# Revit family: Wind_Turbine
name_source: partatom
category: Electrical Equipment
units: mm (PartAtom-declared; Revit-internal decimal feet)

## family parameters
Always vertical = Yes
Classification Number = 23.80.10.11
Cut with Voids When Loaded = No
Maintain Annotation Orientation = No
Panel Configuration = Two Columns, Circuits Across
Part Type = Panelboard
Room Calculation Point = No
Round Connector Dimension = Use Diameter
Shared = No
Work Plane-Based = No

## types (1)
- 3600KW
    Assembly Code = D5090
    Blade Material = ARCAT - Plastic - Glass-Fiber Reinforced - White
    BldCrv = 97' - 4 7/8"
    Construction Details = http://www.arcat.com
    Cut In Wind Speed_MPH = 6.9
    Cut Out Wind Speed_MPH = 60.4
    Default Elevation = 0' - 0"
    Description = 3.6 MW Wind Turbine
    Expected Lifespan (Years) = 25
    Green Building-LEED = http://www.arcat.com
    Hub Material = ARCAT - Metal - Steel 18ga - Painted - White
    Keynote = 13660
    Maintenance Schedule (Months) = 6
    Manufacturer = Generic
    Manufacturer Fax = (203) 939-2444
    Manufacturer Website = http://www.arcat.com
    Model = Generic
    Power Generation_KW = 3600
    Product Data = http://www.arcat.com
    Product Properties = http://www.arcat.com
    Rated Wind Speed_MPH = 14
    Rotor Speed_RPM = 9.1
    Specification = http://www.arcat.com
    Tower Material = ARCAT - Metal - Steel 1/4" - Painted - White
    Warranty Duration (Years) = 5
    Wattage Comments = -3,600,000

## geometry (parser evidence)
native form markers: Sweep x6
no freeform markers — native parametric forms only
